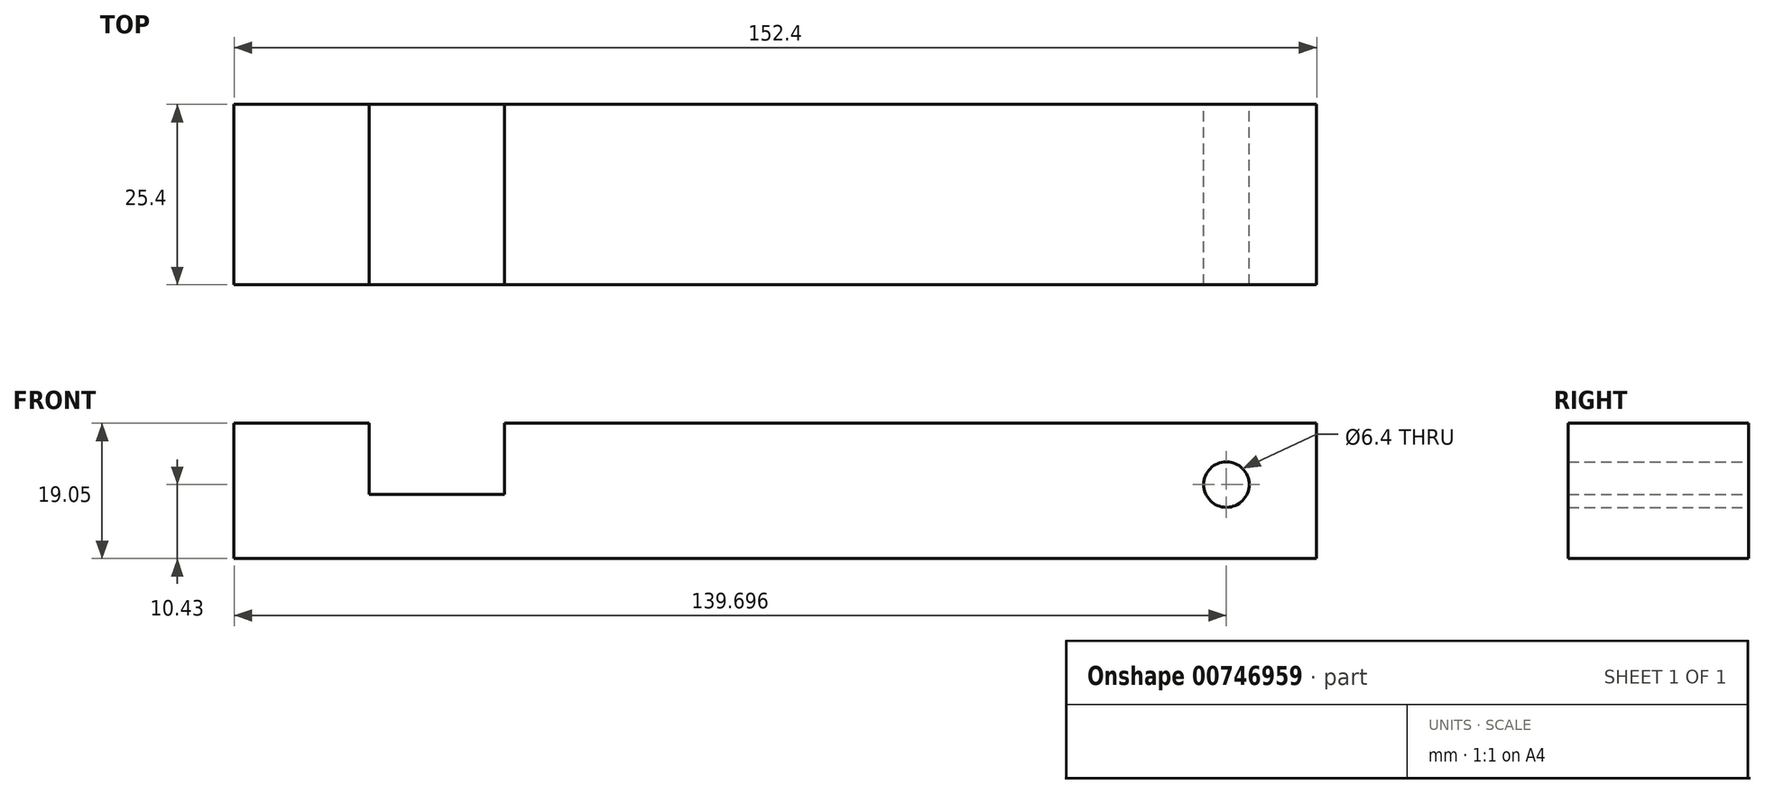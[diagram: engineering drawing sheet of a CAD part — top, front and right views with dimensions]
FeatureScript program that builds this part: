
annotation { "Feature Type Name" : "Feature", "Feature Type Description" : "" }
export const myFeature = defineFeature(function(context is Context, id is Id, definition is map)
    precondition{}
    {
        {
            var Q0;
            Q0=qCreatedBy(makeId("Front.planeOp"),FACE);
            var sketch = newSketch(context, id + "F0", { "sketchPlane" : qUnion([Q0])});
            skLineSegment(sketch, "E0.bottom", {"start": v(171.72, 0) * mm, "end": v(19.32, 0) * mm});
            skLineSegment(sketch, "E0.top", {"start": v(171.72, 19.05) * mm, "end": v(19.32, 19.05) * mm});
            skLineSegment(sketch, "E0.left", {"start": v(171.72, 0) * mm, "end": v(171.72, 19.05) * mm});
            skLineSegment(sketch, "E0.right", {"start": v(19.32, 0) * mm, "end": v(19.32, 19.05) * mm});
            skLineSegment(sketch, "E1.bottom", {"start": v(38.37, 19.05) * mm, "end": v(57.42, 19.05) * mm});
            skLineSegment(sketch, "E1.top", {"start": v(38.37, 9.03) * mm, "end": v(57.42, 9.03) * mm});
            skLineSegment(sketch, "E1.left", {"start": v(38.37, 19.05) * mm, "end": v(38.37, 9.03) * mm});
            skLineSegment(sketch, "E1.right", {"start": v(57.42, 19.05) * mm, "end": v(57.42, 9.03) * mm});
            skCircle(sketch, "E2", {"center": v(159.02, 10.43) * mm, "radius": 3.2 * mm});
            skSolve(sketch);
        }
        {
            var Q0;
            {var subQ7=makeQuery(id+"F0.imprint","IMPRINT",EDGE,{"derivedFrom":sQuery(id+"F0.wireOp",EDGE,"E1.top")});Q0=qUnion([makeQuery(id+"F0.imprint","IMPRINT",FACE,{"disambiguationData":[TD([[subQ7,1.0]])]}),makeQuery(id+"F0.imprint","IMPRINT",FACE,{"disambiguationData":[TD([[makeQuery(id+"F0.imprint","IMPRINT",EDGE,{"derivedFrom":sQuery(id+"F0.wireOp",EDGE,"E0.bottom")}),-1.0]])]})]);}
            extrude(context, id + "F1", {"entities" : qUnion([Q0]), "depth" : 25.4 * mm, "offsetDistance" : 25.4 * mm});
        }
        {
            var Q0;
            Q0=makeQuery(id+"F0.imprint","IMPRINT",FACE,{"disambiguationData":[TD([[makeQuery(id+"F0.imprint","IMPRINT",EDGE,{"derivedFrom":sQuery(id+"F0.wireOp",EDGE,"E1.top")}),1.0]])]});
            extrude(context, id + "F2", {"entities" : qUnion([Q0]), "operationType" : NewBodyOperationType.ADD, "depth" : 19.05 * mm, "offsetDistance" : 25.4 * mm});
        }
        {
            var Q0;
            Q0=makeQuery(id+"F0.imprint","IMPRINT",FACE,{"disambiguationData":[TD([[makeQuery(id+"F0.imprint","IMPRINT",EDGE,{"derivedFrom":sQuery(id+"F0.wireOp",EDGE,"E1.top")}),1.0]])]});
            extrude(context, id + "F3", {"entities" : qUnion([Q0]), "operationType" : NewBodyOperationType.REMOVE, "depth" : 25.4 * mm, "offsetDistance" : 25.4 * mm});
        }
    });
